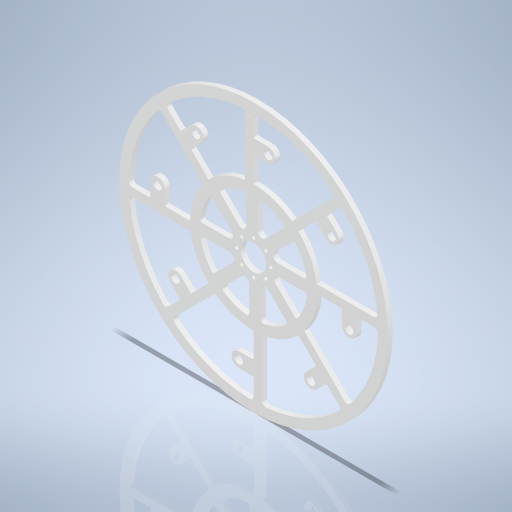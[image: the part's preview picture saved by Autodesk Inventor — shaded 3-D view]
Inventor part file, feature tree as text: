
AUTODESK INVENTOR PART (.ipt)
format: ipt  version: 2024 (Build 280153000, 153)  size: 478,208 bytes
history: native  units: mm
features: sketch x6, extrude x5, pattern_circular x5, fillet x3, hole x1
ambient origin geometry x8: Origin, YZ Plane, XZ Plane, XY Plane, X Axis, Y Axis, Z Axis, Center Point
bodies: Volumenkörper1 (feature_tree)
feature tree (20):
  extrude  "Extrusion1"  Depth=4.0mm TaperAngle=0.0deg
  extrude  "Extrusion2"  TaperAngle=45.0deg  [1 undecoded]
  pattern_circular  "Runde Anordnung1"  Count=5  [1 undecoded]
  extrude  "Extrusion3"  Depth=4.0mm TaperAngle=0.0deg
  hole  "Bohrung1"  [1 undecoded]
  pattern_circular  "Runde Anordnung2"  [2 undecoded]
  extrude  "Extrusion4"  Depth=1.0mm TaperAngle=360.0deg
  fillet  "Rundung1"  Radius=43.0mm
  pattern_circular  "Runde Anordnung3"  [2 undecoded]
  fillet  "Rundung2"  Radius=3.5mm
  pattern_circular  "Runde Anordnung4"  [2 undecoded]
  extrude  "Extrusion5"  Depth=10.0mm TaperAngle=0.0deg
  fillet  "Rundung3"  Radius=2.0mm
  pattern_circular  "Runde Anordnung5"  Count=8 Angle=360.0deg
  sketch  "Skizze1"  dims[d0=220.0mm d1=4.0mm d2=0.0mm]
  sketch  "Skizze2"  dims[d4=7.0mm d6=45.0deg]
  sketch  "Skizze3"  dims[d9=8.0mm d10=50.0mm]
  sketch  "Skizze5"  dims[d11=50.0mm d12=4.0mm d13=0.0mm]
  sketch  "Skizze6"  dims[d14=80.0mm d15=360.0deg d17=21.0mm]
  sketch  "Skizze7"  dims[d18=10.0mm d19=0.0mm d20=28.0mm d21=3.0mm d22=6.0mm d23=4.0mm d24=2.0mm d25=90.0deg d26=8.0mm d27=20.594885mm d28=80.0mm d29=360.0deg d31=43.0mm d33=44.0mm d34=3.5mm d35=3.5mm d36=10.0mm d37=0.0mm d38=2.0mm d39=80.0mm d40=360.0deg d42=3.0mm d43=80.0mm d44=360.0deg d46=6.0mm d47=78.5mm d48=12.0mm d49=7.0mm d50=10.0mm d51=0.0mm d52=1.0mm d53=80.0mm d54=360.0deg]
note: 9 required parameter values undecoded (feature->parameter linkage not recoverable at this tier; creation-order binding heuristic only, values carry confidence <= 0.55)
